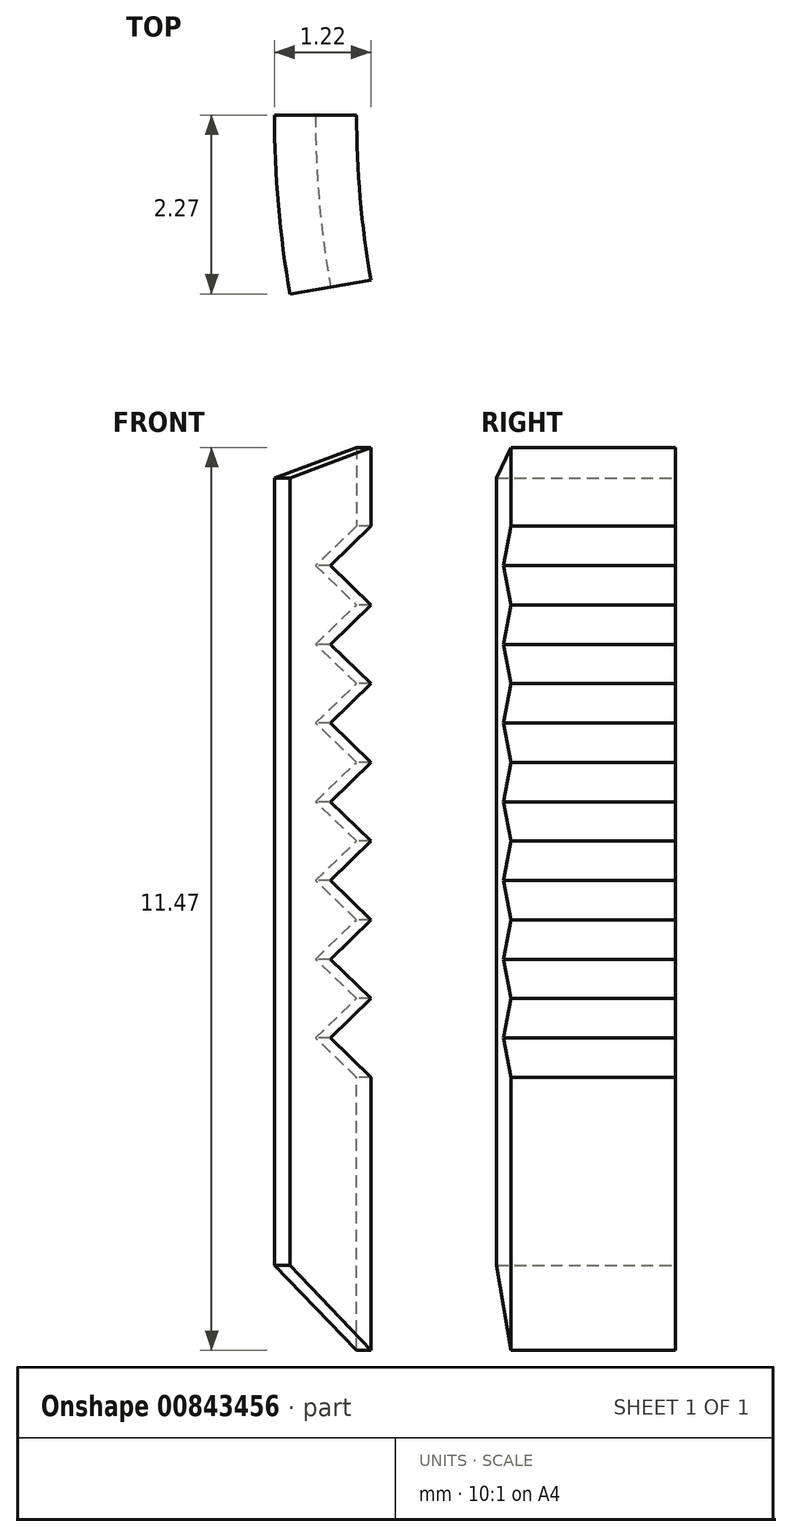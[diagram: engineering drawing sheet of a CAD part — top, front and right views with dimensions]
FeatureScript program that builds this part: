
annotation { "Feature Type Name" : "Feature", "Feature Type Description" : "" }
export const myFeature = defineFeature(function(context is Context, id is Id, definition is map)
    precondition{}
    {
        {
            var Q0;
            Q0=qCreatedBy(makeId("Front.planeOp"),FACE);
            var sketch = newSketch(context, id + "F0", { "sketchPlane" : qUnion([Q0])});
            skLineSegment(sketch, "E0", {"start": v(-24.41, 48.17) * mm, "end": v(-23.37, 48.56) * mm});
            skLineSegment(sketch, "E1", {"start": v(-24.41, 48.17) * mm, "end": v(-24.41, 38.17) * mm});
            skLineSegment(sketch, "E2", {"start": v(-23.37, 37.1) * mm, "end": v(-24.41, 38.17) * mm});
            skLineSegment(sketch, "E3", {"start": v(-23.37, 48.56) * mm, "end": v(-23.37, 47.56) * mm});
            skLineSegment(sketch, "E4", {"start": v(-23.9, 47.06) * mm, "end": v(-23.37, 46.56) * mm});
            skLineSegment(sketch, "E5", {"start": v(-23.37, 47.56) * mm, "end": v(-23.9, 47.06) * mm});
            skLineSegment(sketch, "E6", {"start": v(-23.9, 46.06) * mm, "end": v(-23.37, 46.56) * mm});
            skLineSegment(sketch, "E7", {"start": v(-23.37, 45.56) * mm, "end": v(-23.9, 46.06) * mm});
            skLineSegment(sketch, "E8", {"start": v(-23.9, 45.06) * mm, "end": v(-23.37, 45.56) * mm});
            skLineSegment(sketch, "E9", {"start": v(-23.37, 44.56) * mm, "end": v(-23.9, 45.06) * mm});
            skLineSegment(sketch, "E10", {"start": v(-23.9, 44.06) * mm, "end": v(-23.37, 44.56) * mm});
            skLineSegment(sketch, "E11", {"start": v(-23.37, 43.56) * mm, "end": v(-23.9, 44.06) * mm});
            skLineSegment(sketch, "E12", {"start": v(-23.9, 43.06) * mm, "end": v(-23.37, 43.56) * mm});
            skLineSegment(sketch, "E13", {"start": v(-23.37, 42.56) * mm, "end": v(-23.9, 43.06) * mm});
            skLineSegment(sketch, "E14", {"start": v(-23.9, 42.06) * mm, "end": v(-23.37, 42.56) * mm});
            skLineSegment(sketch, "E15", {"start": v(-23.37, 41.56) * mm, "end": v(-23.9, 42.06) * mm});
            skLineSegment(sketch, "E16", {"start": v(-23.9, 41.06) * mm, "end": v(-23.37, 41.56) * mm});
            skLineSegment(sketch, "E17", {"start": v(-23.37, 40.56) * mm, "end": v(-23.9, 41.06) * mm});
            skLineSegment(sketch, "E18", {"start": v(-23.37, 37.1) * mm, "end": v(-23.37, 40.56) * mm});
            skLineSegment(sketch, "E19", {"start": v(-11.32, 37.1) * mm, "end": v(-11.32, 54.86) * mm});
            skSolve(sketch);
        }
        {
            var Q0;
            Q0 = qSketchRegion(id + "F0", true);
            var Q1;
            Q1=sQuery(id+"F0.wireOp",EDGE,"E19");
            revolve(context, id + "F1", {"surfaceOperationType" : NewSurfaceOperationType.NEW, "entities" : qUnion([Q0]), "axis" : qUnion([Q1]), "revolveType" : RevolveType.ONE_DIRECTION, "angle" : 10 * degree});
        }
    });
